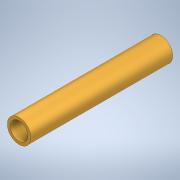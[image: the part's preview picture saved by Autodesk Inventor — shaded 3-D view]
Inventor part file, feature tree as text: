
AUTODESK INVENTOR PART (.ipt)
format: ipt  version: 2020 (Build 240168000, 168)  size: 100,864 bytes
history: native  units: in
note: dims shown in document units (in); Inventor stores cm internally (conversion verified against a paired STEP export)
features: extrude x1, sketch x1
ambient origin geometry x8: Origin, YZ Plane, XZ Plane, XY Plane, X Axis, Y Axis, Z Axis, Center Point
bodies: Body1 (feature_tree)
feature tree (2):
  extrude  "Extrusion2"  Depth=12.0in
  sketch  "Sketch1"  dims[d0=2.0in d3=1.5in d4=12.0in d5=0.0in]
